# Revit family: 2Celite_Embutir_Cuba Redonda_10129
name_source: partatom
category: Plumbing Fixtures
revit_build: Autodesk Revit MEP 2014 (Build: 20131024_2115(x64)
units: mm (PartAtom-declared; Revit-internal decimal feet)

## types (5) — shared parameters
Assembly Code = D2010400
Celite: Categoria = Cubas e Lavatórios
Celite: Código = 10129
Celite: Desenho Técnico = http://www.celite.com.br
Celite: Fabricante = Celite
Celite: Linha = Embutir
Celite: Link do Produto = http://www.celite.com.br
Celite: Norma = ABNT NBR 15097-1: 2011 - Requisitos e métodos de ensaio
Celite: Produto = Louças
Celite: Tipo = Cubas
Celite: Versão = Autodesk Revit MEP 2014
Desenvolvido por = ofcdesk
Diâmetro Ponto de Esgoto = 40 mm
Manufacturer = Celite
Model = 10129
Raio Ponto de Esgoto = 20 mm
Selo de Qualidade ofcdesk = Standard
URL = http://www.celite.com.br
WFU = 2
zero-valued in all types: CWFU, Default Elevation, HWFU

## per-type parameters (varying)
| type | Celite: Cores Disponíveis | Celite: Descrição | Description |
| Branca - 10129 | Branco | Cuba redonda cor branca (10129), linha Embutir - Louças Celite | Cuba redonda cor branca (10129), linha Embutir - Louças Celite |
| Pergamon - 10129 | Pergamon | Cuba redonda cor pergamon (10129), linha Embutir - Louças Celite | Cuba redonda cor pergamon (10129), linha Embutir - Louças Celite |
| Água marinha - 10129 | Água marinha | Cuba redonda cor água marinha (10129), linha Embutir - Louças Celite | Cuba redonda cor água marinha (10129), linha Embutir - Louças Celite |
| Preta - 10129 | Preto | Cuba redonda cor preta (10129), linha Embutir - Louças Celite | Cuba redonda cor preta (10129), linha Embutir - Louças Celite |
| Cinza prata - 10129 | Cinza prata | Cuba redonda cor cinza prata (10129), linha Embutir - Louças Celite | Cuba redonda cor cinza prata (10129), linha Embutir - Louças Celite |

## geometry (parser evidence)
native form markers: Blend x2, Sweep x7
no freeform markers — native parametric forms only
